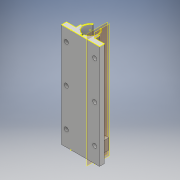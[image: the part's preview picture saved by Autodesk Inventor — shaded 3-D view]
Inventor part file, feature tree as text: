
AUTODESK INVENTOR PART (.ipt)
format: ipt  version: 2017 (Build 210142000, 142)  size: 231,936 bytes
history: native  units: mm
features: sketch x10, extrude x9, projected_geometry x3, other x2
ambient origin geometry x8: Origin, YZ Plane, XZ Plane, XY Plane, X Axis, Y Axis, Z Axis, Center Point
bodies: Solide1 (feature_tree)
feature tree (24):
  extrude  "Extrusion1"  Depth=20.0mm
  extrude  "Extrusion2"  Depth=20.0mm
  extrude  "Extrusion4"  Depth=4.3mm
  extrude  "Extrusion5"  Depth=4.0mm TaperAngle=0.0deg
  extrude  "Extrusion6"  Depth=7.0mm
  extrude  "Extrusion7"  Depth=0.05055mm
  sketch  "Esquisse7"
  extrude  "Extrusion8"  Depth=3.2mm TaperAngle=0.0deg
  extrude  "Extrusion9"  Depth=4.0mm TaperAngle=0.0deg
  extrude  "Extrusion10"  Depth=7.5mm
  sketch  "Esquisse11"
  other  "Plan de construction1"
  other  "Plan de construction2"
  sketch  "Esquisse2"
  projected_geometry  "Boucle projetée1"
  sketch  "Esquisse3"
  sketch  "Esquisse4"
  sketch  "Esquisse5"
  projected_geometry  "Boucle projetée2"
  sketch  "Esquisse6"
  sketch  "Esquisse8"
  sketch  "Esquisse9"
  sketch  "Esquisse10"
  projected_geometry  "Boucle projetée3"
